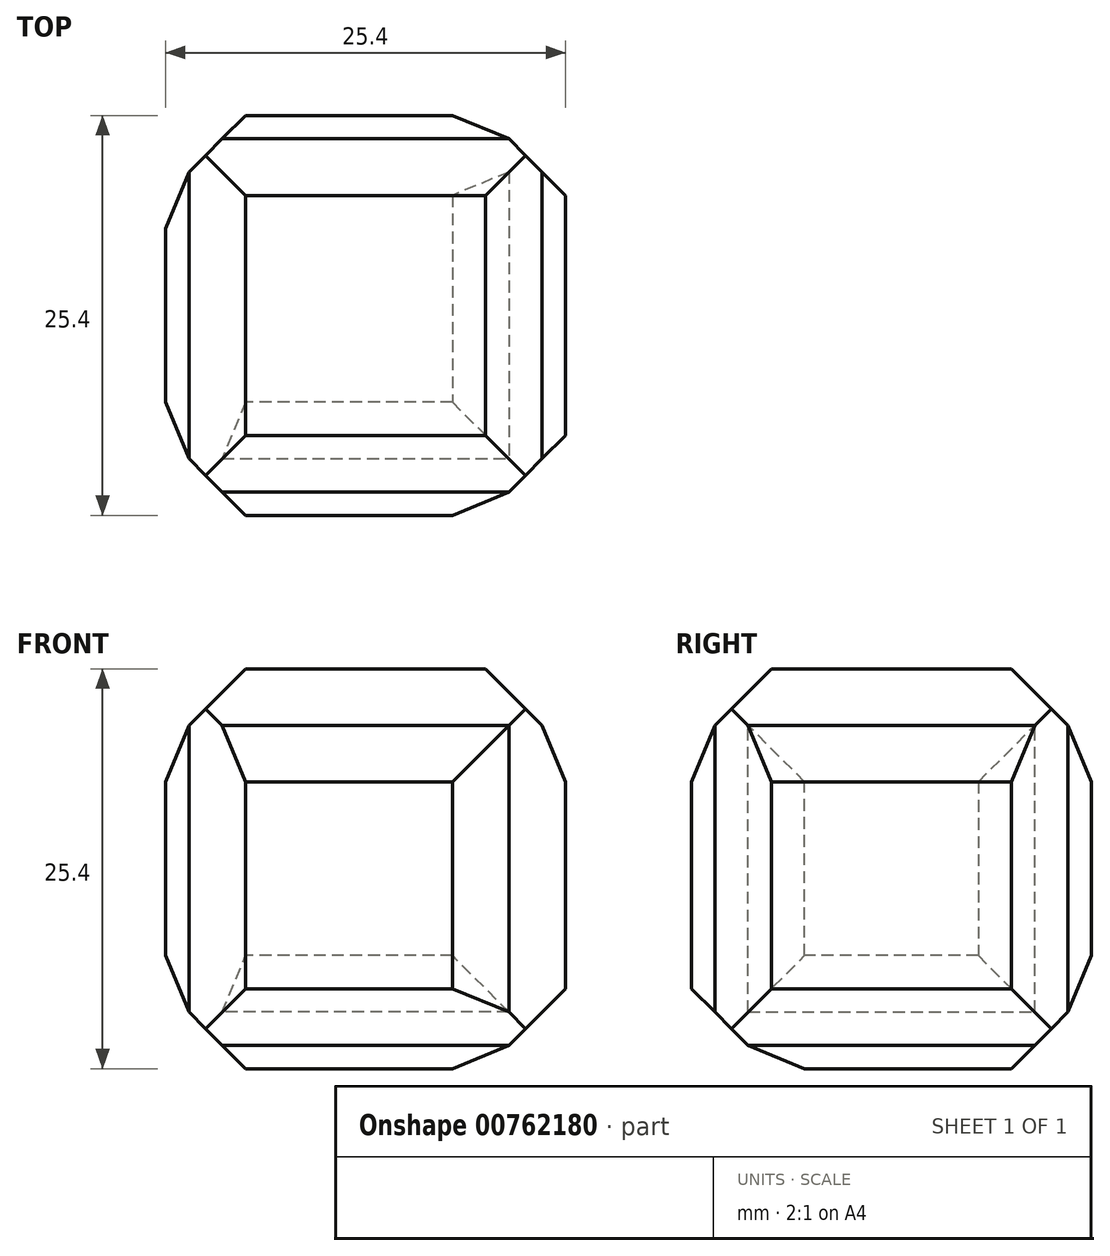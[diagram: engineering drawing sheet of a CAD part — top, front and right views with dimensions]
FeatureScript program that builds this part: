
annotation { "Feature Type Name" : "Feature", "Feature Type Description" : "" }
export const myFeature = defineFeature(function(context is Context, id is Id, definition is map)
    precondition{}
    {
        {
            var Q0;
            Q0=qCreatedBy(makeId("Front.planeOp"),FACE);
            var sketch = newSketch(context, id + "F0", { "sketchPlane" : qUnion([Q0])});
            skLineSegment(sketch, "E0.bottom", {"start": v(0, 0) * mm, "end": v(25.4, 0) * mm});
            skLineSegment(sketch, "E0.top", {"start": v(0, 25.4) * mm, "end": v(25.4, 25.4) * mm});
            skLineSegment(sketch, "E0.left", {"start": v(0, 0) * mm, "end": v(0, 25.4) * mm});
            skLineSegment(sketch, "E0.right", {"start": v(25.4, 0) * mm, "end": v(25.4, 25.4) * mm});
            skSolve(sketch);
        }
        {
            var Q0;
            Q0=makeQuery(id+"F0.imprint","IMPRINT",FACE,{"disambiguationData":[TD([[makeQuery(id+"F0.imprint","IMPRINT",EDGE,{"derivedFrom":sQuery(id+"F0.wireOp",EDGE,"E0.bottom")}),1.0]])]});
            extrude(context, id + "F1", {"entities" : qUnion([Q0]), "depth" : 25.4 * mm, "offsetDistance" : 25.4 * mm});
        }
        {
            var Q0;
            Q0=makeQuery(id+"F1.opExtrude","SWEPT_FACE",FACE,{"disambiguationData":[OSD([sQuery(id+"F0.wireOp",EDGE,"E0.top")])]});
            chamfer(context, id + "F2", {"entities" : qUnion([Q0]), "width" : 5.08 * mm, "tangentPropagation" : true});
        }
        {
            var Q0;
            Q0=makeQuery(id+"F1.opExtrude","SWEPT_FACE",FACE,{"disambiguationData":[OSD([sQuery(id+"F0.wireOp",EDGE,"E0.right")])]});
            chamfer(context, id + "F3", {"entities" : qUnion([Q0]), "width" : 5.08 * mm, "tangentPropagation" : true});
        }
        {
            var Q0;
            Q0=makeQuery(id+"F1.opExtrude","CAP_FACE",FACE,{"disambiguationData":[OSD([sQuery(id+"F0.wireOp",EDGE,"E0.bottom"),sQuery(id+"F0.wireOp",EDGE,"E0.top"),sQuery(id+"F0.wireOp",EDGE,"E0.left"),sQuery(id+"F0.wireOp",EDGE,"E0.right")])],"isStart":false});
            chamfer(context, id + "F4", {"entities" : qUnion([Q0]), "width" : 5.08 * mm, "tangentPropagation" : true});
        }
        {
            var Q0;
            Q0=makeQuery(id+"F1.opExtrude","CAP_EDGE",EDGE,{"disambiguationData":[OSD([sQuery(id+"F0.wireOp",EDGE,"E0.bottom")])],"isStart":true});
            var Q1;
            Q1=makeQuery(id+"F1.opExtrude","SWEPT_FACE",FACE,{"disambiguationData":[OSD([sQuery(id+"F0.wireOp",EDGE,"E0.bottom")])]});
            chamfer(context, id + "F5", {"entities" : qUnion([Q0, Q1]), "width" : 5.08 * mm, "tangentPropagation" : true});
        }
        {
            var Q0;
            Q0=makeQuery(id+"F1.opExtrude","CAP_FACE",FACE,{"disambiguationData":[OSD([sQuery(id+"F0.wireOp",EDGE,"E0.bottom"),sQuery(id+"F0.wireOp",EDGE,"E0.top"),sQuery(id+"F0.wireOp",EDGE,"E0.left"),sQuery(id+"F0.wireOp",EDGE,"E0.right")])],"isStart":true});
            chamfer(context, id + "F6", {"entities" : qUnion([Q0]), "width" : 5.08 * mm, "tangentPropagation" : true});
        }
        {
            var Q0;
            Q0=makeQuery(id+"F1.opExtrude","SWEPT_FACE",FACE,{"disambiguationData":[OSD([sQuery(id+"F0.wireOp",EDGE,"E0.left")])]});
            chamfer(context, id + "F7", {"entities" : qUnion([Q0]), "width" : 5.08 * mm, "tangentPropagation" : true});
        }
    });
